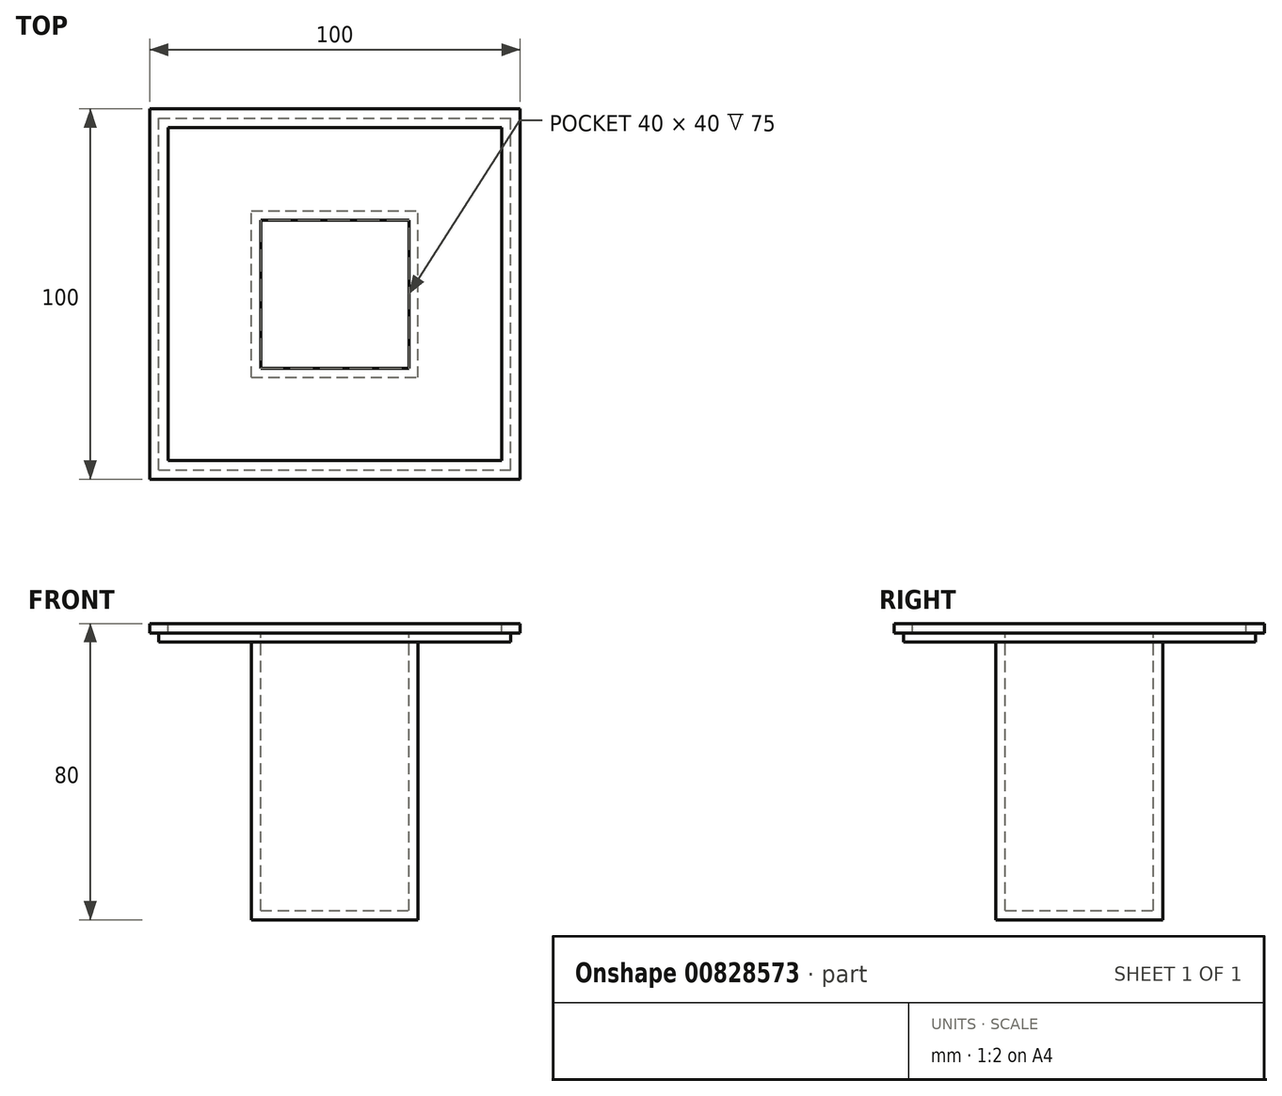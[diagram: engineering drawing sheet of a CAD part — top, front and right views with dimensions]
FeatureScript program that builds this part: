
annotation { "Feature Type Name" : "Feature", "Feature Type Description" : "" }
export const myFeature = defineFeature(function(context is Context, id is Id, definition is map)
    precondition{}
    {
        {
            var Q0;
            Q0=qCreatedBy(makeId("Top.planeOp"),FACE);
            cPlane(context, id + "F0", {"entities" : qUnion([Q0]), "cplaneType" : CPlaneType.OFFSET, "offset" : 80 * mm, "width" : 150 * mm, "height" : 150 * mm});
        }
        {
            var Q0;
            Q0=qCreatedBy(id+"F0.planeOp",FACE);
            var sketch = newSketch(context, id + "F1", { "sketchPlane" : qUnion([Q0])});
            skLineSegment(sketch, "E0.bottom", {"start": v(-50, 50) * mm, "end": v(50, 50) * mm});
            skLineSegment(sketch, "E0.top", {"start": v(-50, -50) * mm, "end": v(50, -50) * mm});
            skLineSegment(sketch, "E0.left", {"start": v(-50, 50) * mm, "end": v(-50, -50) * mm});
            skLineSegment(sketch, "E0.right", {"start": v(50, 50) * mm, "end": v(50, -50) * mm});
            skPoint(sketch, "E0.middle", {"position": v(0, 0) * mm});
            skSolve(sketch);
        }
        {
            var Q0;
            Q0=makeQuery(id+"F1.imprint","IMPRINT",FACE,{"disambiguationData":[TD([[makeQuery(id+"F1.imprint","IMPRINT",EDGE,{"derivedFrom":sQuery(id+"F1.wireOp",EDGE,"E0.bottom")}),-1.0]])]});
            extrude(context, id + "F2", {"entities" : qUnion([Q0]), "oppositeDirection" : true, "depth" : 2.5 * mm, "offsetDistance" : 25 * mm});
        }
        {
            var Q0;
            Q0=qCreatedBy(id+"F0.planeOp",FACE);
            cPlane(context, id + "F3", {"entities" : qUnion([Q0]), "cplaneType" : CPlaneType.OFFSET, "offset" : 2.5 * mm, "oppositeDirection" : true, "width" : 150 * mm, "height" : 150 * mm});
        }
        {
            var Q0;
            Q0=qCreatedBy(id+"F3.planeOp",FACE);
            var sketch = newSketch(context, id + "F4", { "sketchPlane" : qUnion([Q0])});
            skLineSegment(sketch, "E1.bottom", {"start": v(-47.5, -47.5) * mm, "end": v(47.5, -47.5) * mm});
            skLineSegment(sketch, "E1.top", {"start": v(-47.5, 47.5) * mm, "end": v(47.5, 47.5) * mm});
            skLineSegment(sketch, "E1.left", {"start": v(-47.5, -47.5) * mm, "end": v(-47.5, 47.5) * mm});
            skLineSegment(sketch, "E1.right", {"start": v(47.5, -47.5) * mm, "end": v(47.5, 47.5) * mm});
            skPoint(sketch, "E1.middle", {"position": v(0, 0) * mm});
            skSolve(sketch);
        }
        {
            var Q0;
            Q0=makeQuery(id+"F4.imprint","IMPRINT",FACE,{"disambiguationData":[TD([[makeQuery(id+"F4.imprint","IMPRINT",EDGE,{"derivedFrom":sQuery(id+"F4.wireOp",EDGE,"E1.bottom")}),1.0]])]});
            extrude(context, id + "F5", {"entities" : qUnion([Q0]), "operationType" : NewBodyOperationType.ADD, "oppositeDirection" : true, "depth" : 2.5 * mm, "offsetDistance" : 25 * mm});
        }
        {
            var Q0;
            Q0=qCreatedBy(id+"F3.planeOp",FACE);
            cPlane(context, id + "F6", {"entities" : qUnion([Q0]), "cplaneType" : CPlaneType.OFFSET, "offset" : 2.5 * mm, "oppositeDirection" : true, "width" : 150 * mm, "height" : 150 * mm});
        }
        {
            var Q0;
            Q0=qCreatedBy(id+"F6.planeOp",FACE);
            var sketch = newSketch(context, id + "F7", { "sketchPlane" : qUnion([Q0])});
            skLineSegment(sketch, "E2.bottom", {"start": v(-22.5, -22.5) * mm, "end": v(22.5, -22.5) * mm});
            skLineSegment(sketch, "E2.top", {"start": v(-22.5, 22.5) * mm, "end": v(22.5, 22.5) * mm});
            skLineSegment(sketch, "E2.left", {"start": v(-22.5, -22.5) * mm, "end": v(-22.5, 22.5) * mm});
            skLineSegment(sketch, "E2.right", {"start": v(22.5, -22.5) * mm, "end": v(22.5, 22.5) * mm});
            skPoint(sketch, "E2.middle", {"position": v(0, 0) * mm});
            skSolve(sketch);
        }
        {
            var Q0;
            Q0=makeQuery(id+"F7.imprint","IMPRINT",FACE,{"disambiguationData":[TD([[makeQuery(id+"F7.imprint","IMPRINT",EDGE,{"derivedFrom":sQuery(id+"F7.wireOp",EDGE,"E2.bottom")}),1.0]])]});
            extrude(context, id + "F8", {"entities" : qUnion([Q0]), "operationType" : NewBodyOperationType.ADD, "oppositeDirection" : true, "depth" : 75 * mm, "offsetDistance" : 25 * mm});
        }
        {
            var Q0;
            Q0=makeQuery(id+"F2.opExtrude","CAP_FACE",FACE,{"disambiguationData":[OSD([sQuery(id+"F1.wireOp",EDGE,"E0.bottom"),sQuery(id+"F1.wireOp",EDGE,"E0.top"),sQuery(id+"F1.wireOp",EDGE,"E0.left"),sQuery(id+"F1.wireOp",EDGE,"E0.right")])],"isStart":true});
            shell(context, id + "F9", {"entities" : qUnion([Q0]), "thickness" : 2.5 * mm});
        }
    });
